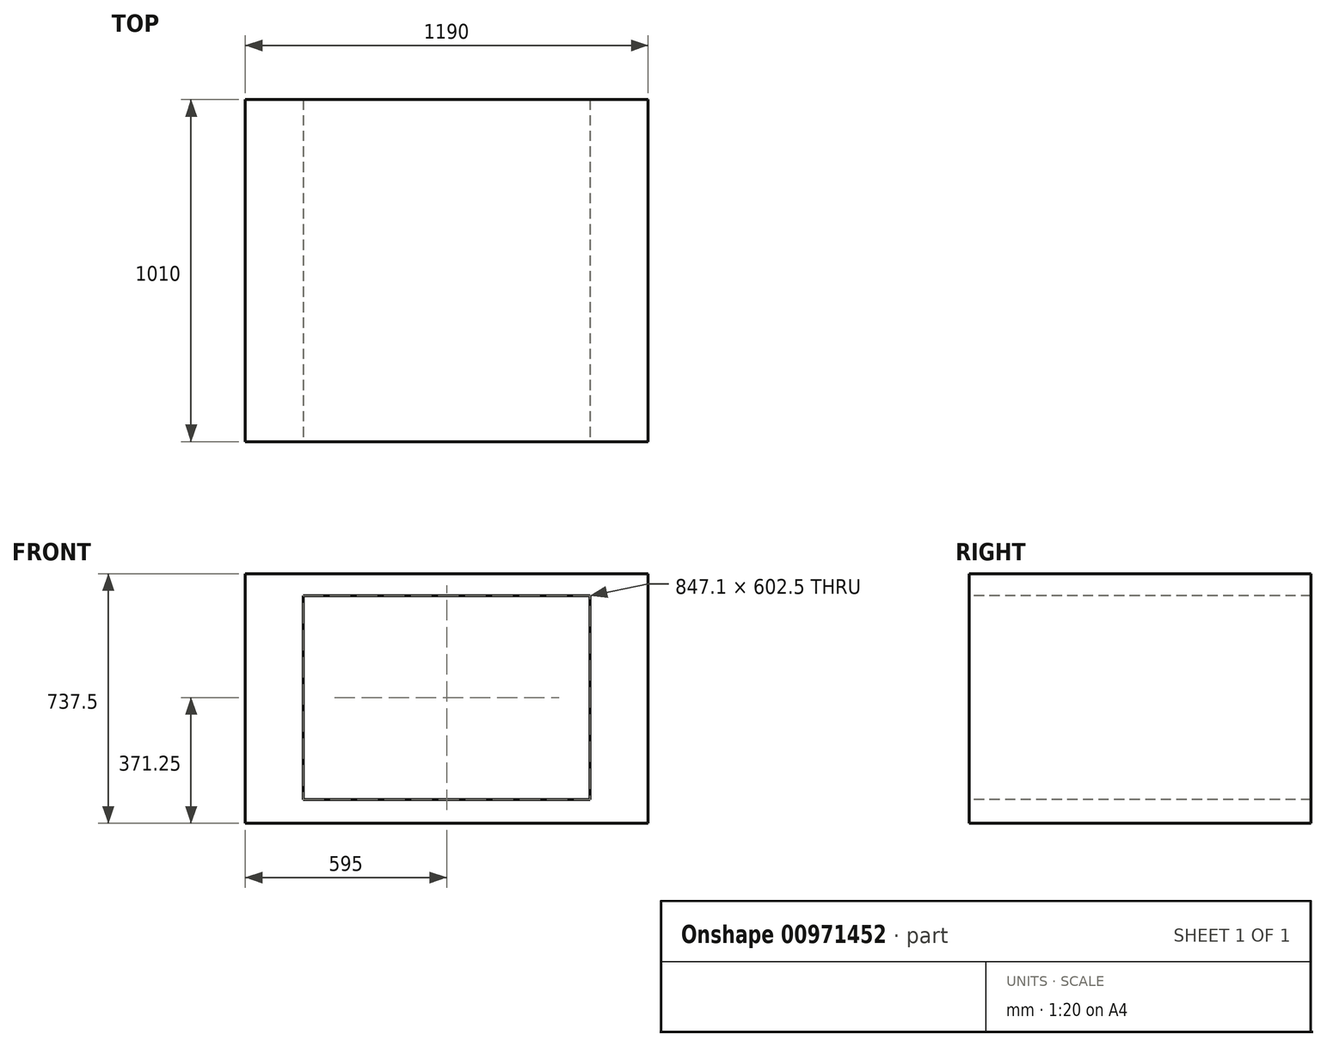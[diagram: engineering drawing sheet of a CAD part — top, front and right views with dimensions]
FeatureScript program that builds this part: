
annotation { "Feature Type Name" : "Feature", "Feature Type Description" : "" }
export const myFeature = defineFeature(function(context is Context, id is Id, definition is map)
    precondition{}
    {
        {
            var Q0;
            Q0=qCreatedBy(makeId("Front.planeOp"),FACE);
            var sketch = newSketch(context, id + "F0", { "sketchPlane" : qUnion([Q0])});
            skLineSegment(sketch, "E0.bottom", {"start": v(-595, -368.75) * mm, "end": v(595, -368.75) * mm});
            skLineSegment(sketch, "E0.top", {"start": v(-595, 368.75) * mm, "end": v(595, 368.75) * mm});
            skLineSegment(sketch, "E0.left", {"start": v(-595, -368.75) * mm, "end": v(-595, 368.75) * mm});
            skLineSegment(sketch, "E0.right", {"start": v(595, -368.75) * mm, "end": v(595, 368.75) * mm});
            skPoint(sketch, "E0.middle", {"position": v(0, 0) * mm});
            skSolve(sketch);
        }
        {
            var Q0;
            Q0 = qSketchRegion(id + "F0", true);
            extrude(context, id + "F1", {"entities" : qUnion([Q0]), "depth" : 1010 * mm, "offsetDistance" : 25.4 * mm});
        }
        {
            var Q0;
            Q0=makeQuery(id+"F1.opExtrude","CAP_FACE",FACE,{"disambiguationData":[OSD([sQuery(id+"F0.wireOp",EDGE,"E0.bottom"),sQuery(id+"F0.wireOp",EDGE,"E0.top"),sQuery(id+"F0.wireOp",EDGE,"E0.left"),sQuery(id+"F0.wireOp",EDGE,"E0.right")])],"isStart":false});
            var sketch = newSketch(context, id + "F2", { "sketchPlane" : qUnion([Q0])});
            skLineSegment(sketch, "E1.top", {"start": v(-423.55, -298.75) * mm, "end": v(423.55, -298.75) * mm});
            skLineSegment(sketch, "E1.left", {"start": v(-423.55, 303.75) * mm, "end": v(-423.55, -298.75) * mm});
            skLineSegment(sketch, "E1.right", {"start": v(423.55, 303.75) * mm, "end": v(423.55, -298.75) * mm});
            skPoint(sketch, "E1.middle", {"position": v(0, 2.5) * mm});
            skLineSegment(sketch, "E2", {"start": v(423.55, 303.75) * mm, "end": v(-423.55, 303.75) * mm});
            skSolve(sketch);
        }
        {
            var Q0;
            Q0 = qSketchRegion(id + "F2", true);
            extrude(context, id + "F3", {"entities" : qUnion([Q0]), "operationType" : NewBodyOperationType.REMOVE, "endBound" : BoundingType.THROUGH_ALL, "oppositeDirection" : true, "depth" : 25.4 * mm, "offsetDistance" : 25.4 * mm});
        }
    });
